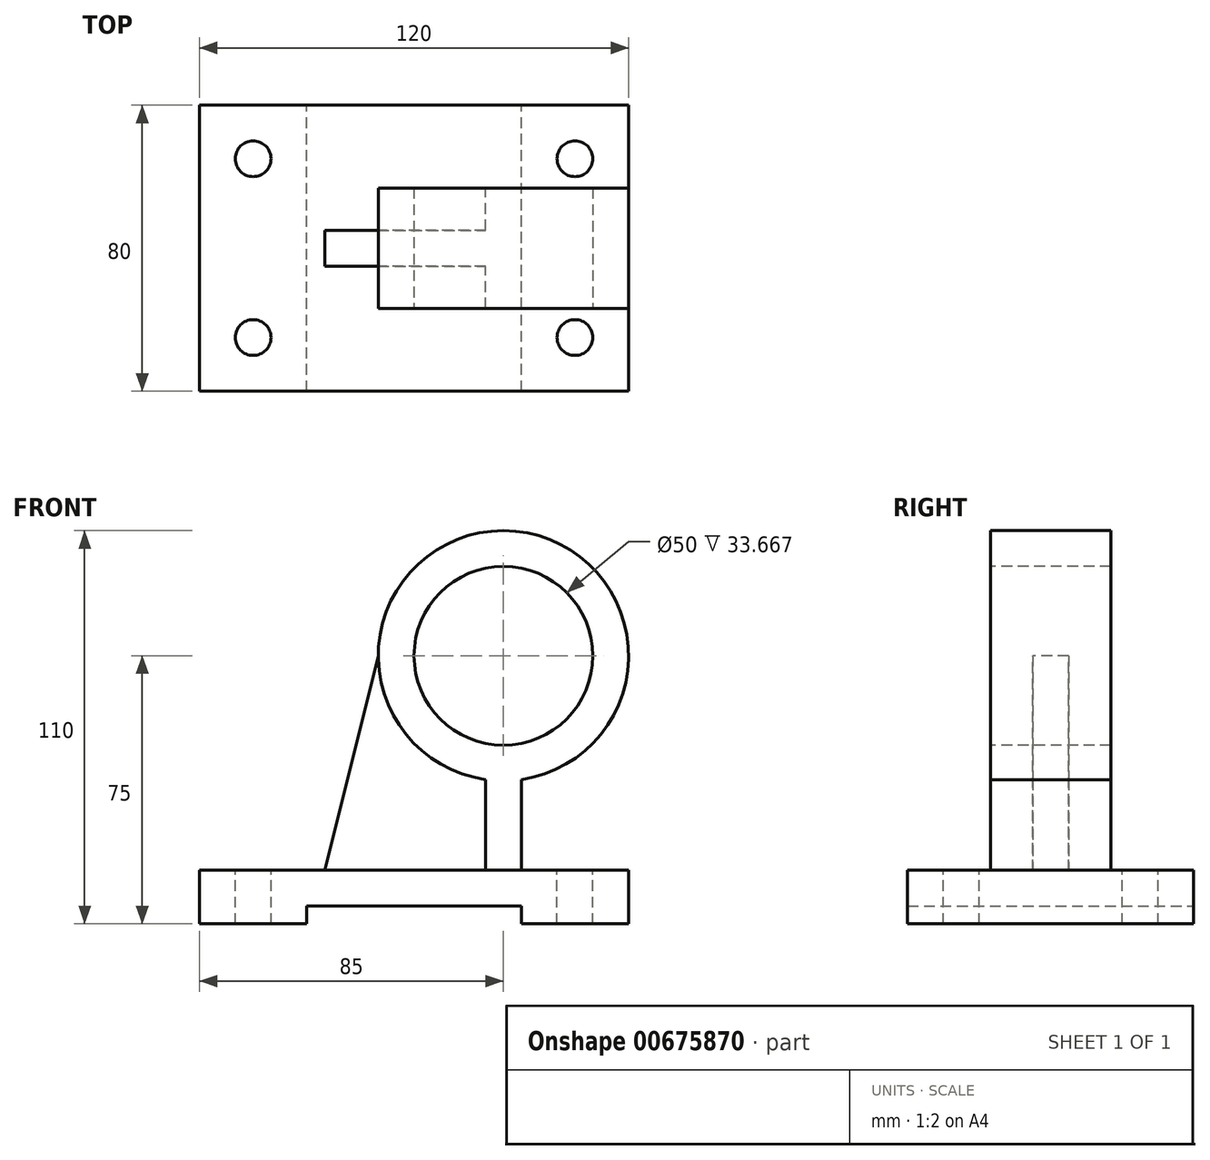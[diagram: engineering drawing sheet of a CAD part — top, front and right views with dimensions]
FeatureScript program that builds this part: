
annotation { "Feature Type Name" : "Feature", "Feature Type Description" : "" }
export const myFeature = defineFeature(function(context is Context, id is Id, definition is map)
    precondition{}
    {
        {
            var Q0;
            Q0=qCreatedBy(makeId("Front.planeOp"),FACE);
            var sketch = newSketch(context, id + "F0", { "sketchPlane" : qUnion([Q0])});
            skLineSegment(sketch, "E0", {"start": v(0, 0) * mm, "end": v(120, 0) * mm});
            skLineSegment(sketch, "E1", {"start": v(120, 0) * mm, "end": v(120, -15) * mm});
            skLineSegment(sketch, "E2", {"start": v(120, -15) * mm, "end": v(90, -15) * mm});
            skLineSegment(sketch, "E3", {"start": v(30, -10) * mm, "end": v(30, -15) * mm});
            skLineSegment(sketch, "E4", {"start": v(30, -15) * mm, "end": v(0, -15) * mm});
            skLineSegment(sketch, "E5", {"start": v(0, -15) * mm, "end": v(0, 0) * mm});
            skLineSegment(sketch, "E6", {"start": v(90, -15) * mm, "end": v(90, -10) * mm});
            skLineSegment(sketch, "E7", {"start": v(30, -10) * mm, "end": v(90, -10) * mm});
            skSolve(sketch);
        }
        {
            var Q0;
            Q0 = qSketchRegion(id + "F0", true);
            extrude(context, id + "F1", {"entities" : qUnion([Q0]), "depth" : 80 * mm, "offsetDistance" : 25 * mm});
        }
        {
            var Q0;
            Q0=makeQuery(id+"F1.opExtrude","SWEPT_FACE",FACE,{"disambiguationData":[OSD([sQuery(id+"F0.wireOp",EDGE,"E0")])]});
            var sketch = newSketch(context, id + "F2", { "sketchPlane" : qUnion([Q0])});
            skCircle(sketch, "E8", {"center": v(15, -15) * mm, "radius": 5 * mm});
            skCircle(sketch, "E9", {"center": v(15, -65) * mm, "radius": 5 * mm});
            skCircle(sketch, "E10", {"center": v(105, -65) * mm, "radius": 5 * mm});
            skCircle(sketch, "E11", {"center": v(105, -15) * mm, "radius": 5 * mm});
            skPoint(sketch, "E12", {"position": v(60, -40) * mm});
            skPoint(sketch, "E12.positionSnap0", {"position": v(0, -40) * mm});
            skPoint(sketch, "E12.positionSnap1", {"position": v(60, 0) * mm});
            skLineSegment(sketch, "E13", {"start": v(0, -40) * mm, "end": v(120, -40) * mm});
            skLineSegment(sketch, "E14", {"start": v(60, 0) * mm, "end": v(60, -80) * mm});
            skSolve(sketch);
        }
        {
            var Q0;
            Q0 = qSketchRegion(id + "F2", true);
            extrude(context, id + "F3", {"entities" : qUnion([Q0]), "operationType" : NewBodyOperationType.REMOVE, "oppositeDirection" : true, "depth" : 25 * mm, "offsetDistance" : 25 * mm});
        }
        {
            var Q0;
            Q0=makeQuery(id+"F1.opExtrude","SWEPT_FACE",FACE,{"disambiguationData":[OSD([sQuery(id+"F0.wireOp",EDGE,"E0")])]});
            var sketch = newSketch(context, id + "F4", { "sketchPlane" : qUnion([Q0])});
            skLineSegment(sketch, "E15", {"start": v(0, -40) * mm, "end": v(62.5, -40) * mm, "construction": true});
            skLineSegment(sketch, "E16.bottom", {"start": v(80, -45) * mm, "end": v(35, -45) * mm});
            skLineSegment(sketch, "E16.top", {"start": v(80, -35) * mm, "end": v(35, -35) * mm});
            skLineSegment(sketch, "E16.left", {"start": v(90, -45) * mm, "end": v(90, -35) * mm});
            skLineSegment(sketch, "E16.right", {"start": v(35, -45) * mm, "end": v(35, -35) * mm});
            skPoint(sketch, "E16.middle", {"position": v(62.5, -40) * mm});
            skLineSegment(sketch, "E17.bottom", {"start": v(90, -56.83) * mm, "end": v(80, -56.83) * mm});
            skLineSegment(sketch, "E17.top", {"start": v(90, -23.17) * mm, "end": v(80, -23.17) * mm});
            skLineSegment(sketch, "E17.left", {"start": v(90, -56.83) * mm, "end": v(90, -23.17) * mm});
            skLineSegment(sketch, "E17.right", {"start": v(80, -56.83) * mm, "end": v(80, -45) * mm});
            skPoint(sketch, "E17.middle", {"position": v(85, -40) * mm});
            skPoint(sketch, "E17.cornerSnap0", {"position": v(90, -40) * mm});
            skLineSegment(sketch, "E18.trimOffspring", {"start": v(80, -35) * mm, "end": v(80, -23.17) * mm});
            skLineSegment(sketch, "E19.trimOffspring", {"start": v(85, -40) * mm, "end": v(120, -40) * mm, "construction": true});
            skSolve(sketch);
        }
        {
            var Q0;
            Q0=makeQuery(id+"F4.imprint","IMPRINT",FACE,{"disambiguationData":[TD([[makeQuery(id+"F4.imprint","IMPRINT",EDGE,{"derivedFrom":sQuery(id+"F4.wireOp",EDGE,"E16.bottom")}),-1.0]])]});
            extrude(context, id + "F5", {"entities" : qUnion([Q0]), "operationType" : NewBodyOperationType.ADD, "depth" : 60 * mm, "offsetDistance" : 25 * mm});
        }
        {
            var Q0;
            Q0=makeQuery(id+"F5.opExtrude","SWEPT_FACE",FACE,{"disambiguationData":[OSD([sQuery(id+"F4.wireOp",EDGE,"E17.bottom")])]});
            var sketch = newSketch(context, id + "F6", { "sketchPlane" : qUnion([Q0])});
            skCircle(sketch, "E20", {"center": v(85, 60) * mm, "radius": 35 * mm});
            skSolve(sketch);
        }
        {
            var Q0;
            Q0 = qSketchRegion(id + "F6", true);
            var Q1;
            Q1=makeQuery(id+"F5.opExtrude","SWEPT_FACE",FACE,{"disambiguationData":[OSD([sQuery(id+"F4.wireOp",EDGE,"E17.top")])]});
            extrude(context, id + "F7", {"entities" : qUnion([Q0]), "operationType" : NewBodyOperationType.ADD, "endBound" : BoundingType.UP_TO_SURFACE, "oppositeDirection" : true, "depth" : 25 * mm, "endBoundEntityFace" : qUnion([Q1]), "offsetDistance" : 25 * mm});
        }
        {
            var Q0;
            Q0=makeQuery(id+"F7.boolean.opBoolean","MERGE",FACE,{"derivedFrom":[makeQuery(id+"F5.opExtrude","SWEPT_FACE",FACE,{"disambiguationData":[OSD([sQuery(id+"F4.wireOp",EDGE,"E17.bottom")])]}),makeQuery(id+"F7.opExtrude","CAP_FACE",FACE,{"disambiguationData":[OSD([sQuery(id+"F6.wireOp",EDGE,"E20")])],"isStart":true})]});
            var sketch = newSketch(context, id + "F8", { "sketchPlane" : qUnion([Q0])});
            skCircle(sketch, "E21", {"center": v(85, 60) * mm, "radius": 25 * mm});
            skSolve(sketch);
        }
        {
            var Q0;
            Q0=makeQuery(id+"F8.imprint","IMPRINT",FACE,{"disambiguationData":[TD([[makeQuery(id+"F8.imprint","IMPRINT",EDGE,{"derivedFrom":sQuery(id+"F8.wireOp",EDGE,"E21")}),1.0]])]});
            extrude(context, id + "F9", {"entities" : qUnion([Q0]), "operationType" : NewBodyOperationType.REMOVE, "oppositeDirection" : true, "depth" : 52.6 * mm, "offsetDistance" : 25 * mm});
        }
        {
            var Q0;
            Q0=makeQuery(id+"F5.opExtrude","SWEPT_FACE",FACE,{"disambiguationData":[OSD([sQuery(id+"F4.wireOp",EDGE,"E16.bottom")])]});
            var sketch = newSketch(context, id + "F10", { "sketchPlane" : qUnion([Q0])});
            skLineSegment(sketch, "E22", {"start": v(35, 0) * mm, "end": v(50, 60) * mm});
            skLineSegment(sketch, "E23", {"start": v(50, 60) * mm, "end": v(35, 60) * mm});
            skLineSegment(sketch, "E24", {"start": v(35, 60) * mm, "end": v(35, 0) * mm});
            skSolve(sketch);
        }
        {
            var Q0;
            Q0=makeQuery(id+"F10.imprint","IMPRINT",FACE,{"disambiguationData":[TD([[makeQuery(id+"F10.imprint","IMPRINT",EDGE,{"derivedFrom":sQuery(id+"F10.wireOp",EDGE,"E22")}),1.0]])]});
            extrude(context, id + "F11", {"entities" : qUnion([Q0]), "operationType" : NewBodyOperationType.REMOVE, "oppositeDirection" : true, "depth" : 25 * mm, "offsetDistance" : 25 * mm});
        }
    });
